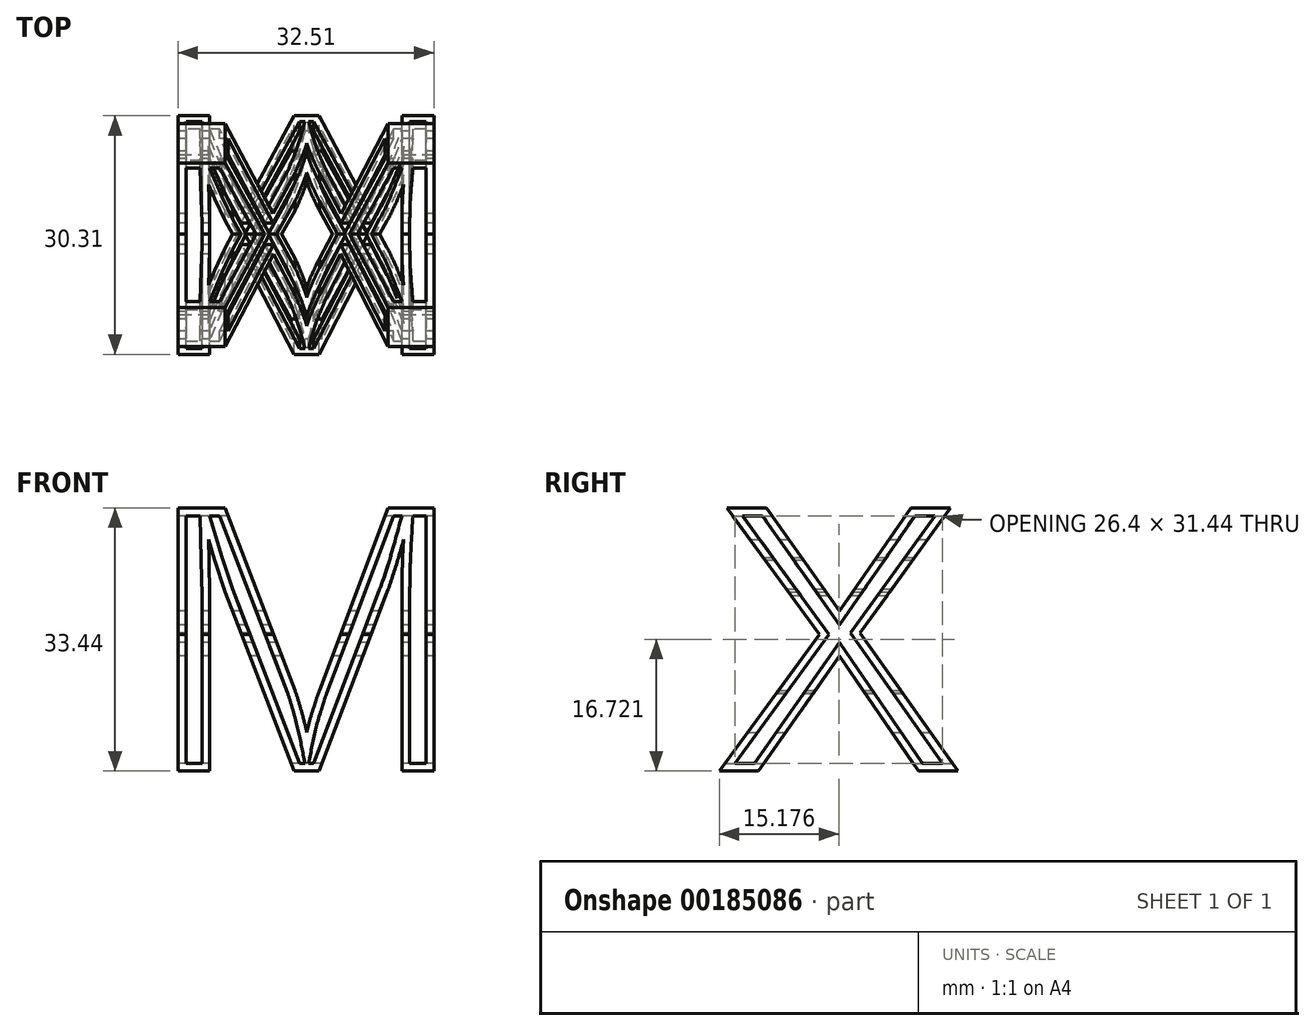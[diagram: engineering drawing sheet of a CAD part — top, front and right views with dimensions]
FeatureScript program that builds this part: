
annotation { "Feature Type Name" : "Feature", "Feature Type Description" : "" }
export const myFeature = defineFeature(function(context is Context, id is Id, definition is map)
    precondition{}
    {
        {
            var Q0;
            Q0=qCreatedBy(makeId("Front.planeOp"),FACE);
            var sketch = newSketch(context, id + "F0", { "sketchPlane" : qUnion([Q0])});
            skText(sketch, "E0", { "text": "M", "fontName": "Arimo-Regular.ttf"});
            skLineSegment(sketch, "E1", {"start": v(-19.94, 0) * mm, "end": v(19.94, 0) * mm, "construction": true});
            skPoint(sketch, "E2", {"position": v(0, 0) * mm});
            const initialGuessF0  = {"E0": [-0.01994, -0.0175, 1, 0, 0.035]};
            skSetInitialGuess(sketch, initialGuessF0);
            skSolve(sketch);
        }
        {
            var Q0;
            Q0=qCreatedBy(makeId("Right.planeOp"),FACE);
            var sketch = newSketch(context, id + "F1", { "sketchPlane" : qUnion([Q0])});
            skText(sketch, "E3", { "text": "X", "fontName": "Arimo-Regular.ttf"});
            skPoint(sketch, "E4", {"position": v(0, 0) * mm});
            const initialGuessF1  = {"E3": [-0.01739, -0.0175, 1, 0, 0.035]};
            skSetInitialGuess(sketch, initialGuessF1);
            skSolve(sketch);
        }
        {
            var Q0;
            Q0=qSketchRegion(id+"F0",true);
            extrude(context, id + "F2", {"entities" : qUnion([Q0]), "depth" : 50 * mm, "hasSecondDirection" : true, "secondDirectionOppositeDirection" : true, "secondDirectionDepth" : 50 * mm});
        }
        {
            var Q0;
            Q0=qSketchRegion(id+"F1",true);
            extrude(context, id + "F3", {"entities" : qUnion([Q0]), "depth" : 50 * mm, "hasSecondDirection" : true, "secondDirectionOppositeDirection" : true, "secondDirectionDepth" : 50 * mm});
        }
        {
            var Q0;
            Q0=makeQuery(id+"F2.opExtrude","CAP_FACE",FACE,{"disambiguationData":[OSD([sQuery(id+"F0.wireOp",EDGE,"E0.sketch_text.stroke-0"),sQuery(id+"F0.wireOp",EDGE,"E0.sketch_text.stroke-1"),sQuery(id+"F0.wireOp",EDGE,"E0.sketch_text.stroke-2"),sQuery(id+"F0.wireOp",EDGE,"E0.sketch_text.stroke-3"),sQuery(id+"F0.wireOp",EDGE,"E0.sketch_text.stroke-4"),sQuery(id+"F0.wireOp",EDGE,"E0.sketch_text.stroke-5"),sQuery(id+"F0.wireOp",EDGE,"E0.sketch_text.stroke-6"),sQuery(id+"F0.wireOp",EDGE,"E0.sketch_text.stroke-7"),sQuery(id+"F0.wireOp",EDGE,"E0.sketch_text.stroke-8"),sQuery(id+"F0.wireOp",EDGE,"E0.sketch_text.stroke-9"),sQuery(id+"F0.wireOp",EDGE,"E0.sketch_text.stroke-10"),sQuery(id+"F0.wireOp",EDGE,"E0.sketch_text.stroke-11"),sQuery(id+"F0.wireOp",EDGE,"E0.sketch_text.stroke-12"),sQuery(id+"F0.wireOp",EDGE,"E0.sketch_text.stroke-13"),sQuery(id+"F0.wireOp",EDGE,"E0.sketch_text.stroke-14"),sQuery(id+"F0.wireOp",EDGE,"E0.sketch_text.stroke-15"),sQuery(id+"F0.wireOp",EDGE,"E0.sketch_text.stroke-16"),sQuery(id+"F0.wireOp",EDGE,"E0.sketch_text.stroke-17"),sQuery(id+"F0.wireOp",EDGE,"E0.sketch_text.stroke-18"),sQuery(id+"F0.wireOp",EDGE,"E0.sketch_text.stroke-19"),sQuery(id+"F0.wireOp",EDGE,"E0.sketch_text.stroke-20"),sQuery(id+"F0.wireOp",EDGE,"E0.sketch_text.stroke-21"),sQuery(id+"F0.wireOp",EDGE,"E0.sketch_text.stroke-22")])],"isStart":false});
            shell(context, id + "F4", {"entities" : qUnion([Q0]), "thickness" : 1 * mm});
        }
        {
            var Q0;
            Q0=makeQuery(id+"F3.opExtrude","CAP_FACE",FACE,{"disambiguationData":[OSD([sQuery(id+"F1.wireOp",EDGE,"E3.sketch_text.stroke-0"),sQuery(id+"F1.wireOp",EDGE,"E3.sketch_text.stroke-1"),sQuery(id+"F1.wireOp",EDGE,"E3.sketch_text.stroke-2"),sQuery(id+"F1.wireOp",EDGE,"E3.sketch_text.stroke-3"),sQuery(id+"F1.wireOp",EDGE,"E3.sketch_text.stroke-4"),sQuery(id+"F1.wireOp",EDGE,"E3.sketch_text.stroke-5"),sQuery(id+"F1.wireOp",EDGE,"E3.sketch_text.stroke-6"),sQuery(id+"F1.wireOp",EDGE,"E3.sketch_text.stroke-7"),sQuery(id+"F1.wireOp",EDGE,"E3.sketch_text.stroke-8"),sQuery(id+"F1.wireOp",EDGE,"E3.sketch_text.stroke-9"),sQuery(id+"F1.wireOp",EDGE,"E3.sketch_text.stroke-10"),sQuery(id+"F1.wireOp",EDGE,"E3.sketch_text.stroke-11"),sQuery(id+"F1.wireOp",EDGE,"E3.sketch_text.stroke-12"),sQuery(id+"F1.wireOp",EDGE,"E3.sketch_text.stroke-13"),sQuery(id+"F1.wireOp",EDGE,"E3.sketch_text.stroke-14")])],"isStart":false});
            shell(context, id + "F5", {"entities" : qUnion([Q0]), "thickness" : 1 * mm});
        }
        {
            var Q0;
            Q0=makeQuery(id+"F2.opExtrude","SWEPT_BODY",BODY,{"disambiguationData":[OSD([sQuery(id+"F0.wireOp",EDGE,"E0.sketch_text.stroke-0"),sQuery(id+"F0.wireOp",EDGE,"E0.sketch_text.stroke-1"),sQuery(id+"F0.wireOp",EDGE,"E0.sketch_text.stroke-2"),sQuery(id+"F0.wireOp",EDGE,"E0.sketch_text.stroke-3"),sQuery(id+"F0.wireOp",EDGE,"E0.sketch_text.stroke-4"),sQuery(id+"F0.wireOp",EDGE,"E0.sketch_text.stroke-5"),sQuery(id+"F0.wireOp",EDGE,"E0.sketch_text.stroke-6"),sQuery(id+"F0.wireOp",EDGE,"E0.sketch_text.stroke-7"),sQuery(id+"F0.wireOp",EDGE,"E0.sketch_text.stroke-8"),sQuery(id+"F0.wireOp",EDGE,"E0.sketch_text.stroke-9"),sQuery(id+"F0.wireOp",EDGE,"E0.sketch_text.stroke-10"),sQuery(id+"F0.wireOp",EDGE,"E0.sketch_text.stroke-11"),sQuery(id+"F0.wireOp",EDGE,"E0.sketch_text.stroke-12"),sQuery(id+"F0.wireOp",EDGE,"E0.sketch_text.stroke-13"),sQuery(id+"F0.wireOp",EDGE,"E0.sketch_text.stroke-14"),sQuery(id+"F0.wireOp",EDGE,"E0.sketch_text.stroke-15"),sQuery(id+"F0.wireOp",EDGE,"E0.sketch_text.stroke-16"),sQuery(id+"F0.wireOp",EDGE,"E0.sketch_text.stroke-17"),sQuery(id+"F0.wireOp",EDGE,"E0.sketch_text.stroke-18"),sQuery(id+"F0.wireOp",EDGE,"E0.sketch_text.stroke-19"),sQuery(id+"F0.wireOp",EDGE,"E0.sketch_text.stroke-20"),sQuery(id+"F0.wireOp",EDGE,"E0.sketch_text.stroke-21"),sQuery(id+"F0.wireOp",EDGE,"E0.sketch_text.stroke-22")])]});
            var Q1;
            Q1=makeQuery(id+"F3.opExtrude","SWEPT_BODY",BODY,{"disambiguationData":[OSD([sQuery(id+"F1.wireOp",EDGE,"E3.sketch_text.stroke-0"),sQuery(id+"F1.wireOp",EDGE,"E3.sketch_text.stroke-1"),sQuery(id+"F1.wireOp",EDGE,"E3.sketch_text.stroke-2"),sQuery(id+"F1.wireOp",EDGE,"E3.sketch_text.stroke-3"),sQuery(id+"F1.wireOp",EDGE,"E3.sketch_text.stroke-4"),sQuery(id+"F1.wireOp",EDGE,"E3.sketch_text.stroke-5"),sQuery(id+"F1.wireOp",EDGE,"E3.sketch_text.stroke-6"),sQuery(id+"F1.wireOp",EDGE,"E3.sketch_text.stroke-7"),sQuery(id+"F1.wireOp",EDGE,"E3.sketch_text.stroke-8"),sQuery(id+"F1.wireOp",EDGE,"E3.sketch_text.stroke-9"),sQuery(id+"F1.wireOp",EDGE,"E3.sketch_text.stroke-10"),sQuery(id+"F1.wireOp",EDGE,"E3.sketch_text.stroke-11"),sQuery(id+"F1.wireOp",EDGE,"E3.sketch_text.stroke-12"),sQuery(id+"F1.wireOp",EDGE,"E3.sketch_text.stroke-13"),sQuery(id+"F1.wireOp",EDGE,"E3.sketch_text.stroke-14")])]});
            booleanBodies(context, id + "F6", {"operationType" : BooleanOperationType.INTERSECTION, "tools" : qUnion([Q0, Q1])});
        }
    });
